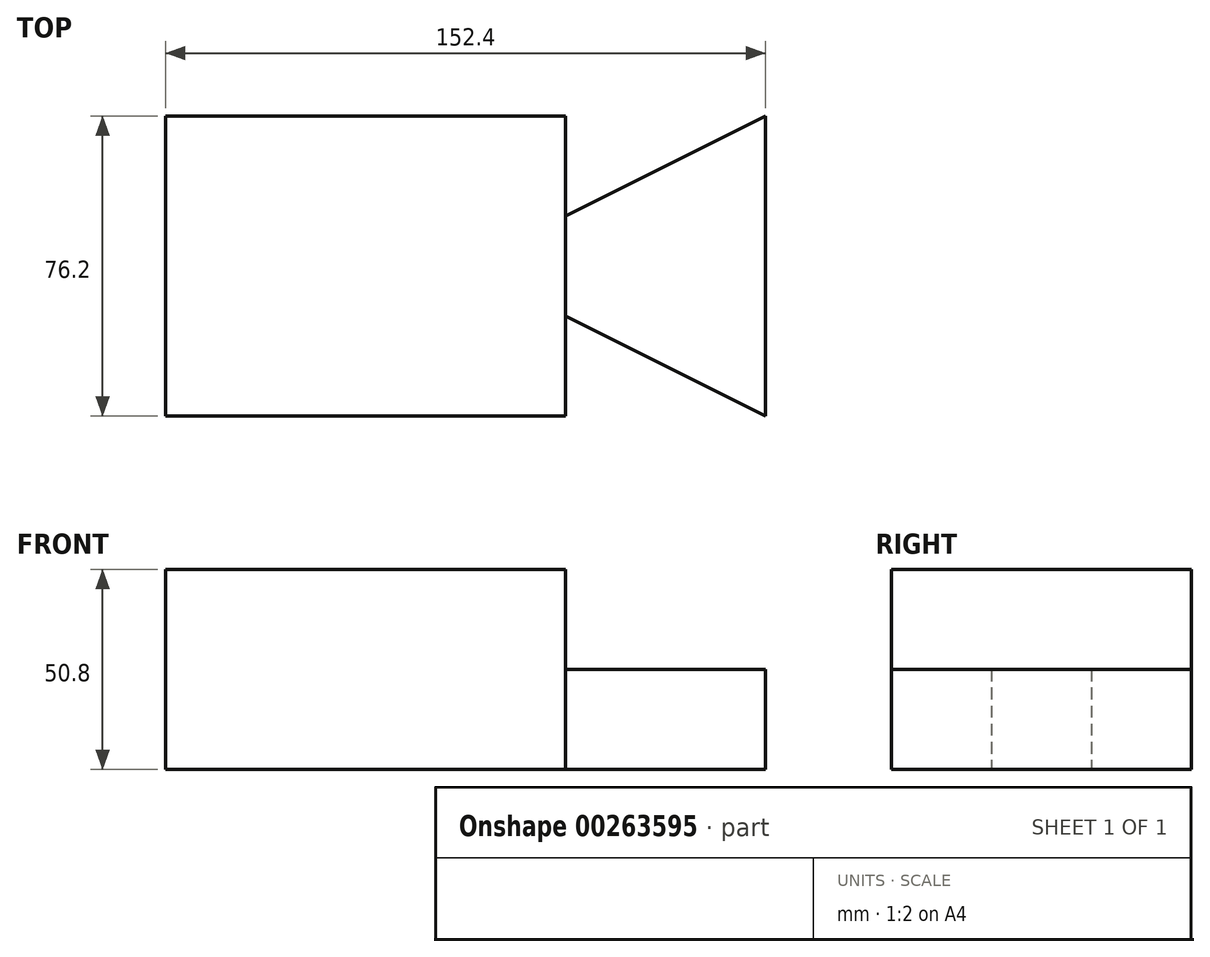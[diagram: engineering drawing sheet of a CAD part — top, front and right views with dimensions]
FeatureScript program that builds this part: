
annotation { "Feature Type Name" : "Feature", "Feature Type Description" : "" }
export const myFeature = defineFeature(function(context is Context, id is Id, definition is map)
    precondition{}
    {
        {
            var Q0;
            Q0=qCreatedBy(makeId("Front.planeOp"),FACE);
            var sketch = newSketch(context, id + "F0", { "sketchPlane" : qUnion([Q0])});
            skLineSegment(sketch, "E0", {"start": v(-72.92, 0) * mm, "end": v(-72.92, 50.8) * mm});
            skLineSegment(sketch, "E1", {"start": v(-72.92, 50.8) * mm, "end": v(28.68, 50.8) * mm});
            skLineSegment(sketch, "E2", {"start": v(-72.92, 0) * mm, "end": v(28.68, 0) * mm});
            skLineSegment(sketch, "E3", {"start": v(28.68, 0) * mm, "end": v(28.68, 25.4) * mm});
            skLineSegment(sketch, "E4", {"start": v(28.68, 50.8) * mm, "end": v(28.68, 25.4) * mm});
            skLineSegment(sketch, "E5", {"start": v(28.68, 25.4) * mm, "end": v(28.68, 50.8) * mm});
            skSolve(sketch);
        }
        {
            var Q0;
            Q0 = qSketchRegion(id + "F0", true);
            extrude(context, id + "F1", {"entities" : qUnion([Q0]), "depth" : 76.2 * mm});
        }
        {
            var Q0;
            Q0=makeQuery(id+"F1.opExtrude","SWEPT_FACE",FACE,{"disambiguationData":[OSD([sQuery(id+"F0.wireOp",EDGE,"E2")])]});
            var sketch = newSketch(context, id + "F2", { "sketchPlane" : qUnion([Q0])});
            skLineSegment(sketch, "E6", {"start": v(28.68, 0) * mm, "end": v(28.68, 25.4) * mm, "construction": true});
            skLineSegment(sketch, "E7", {"start": v(28.68, 76.2) * mm, "end": v(28.68, 50.8) * mm, "construction": true});
            skLineSegment(sketch, "E8", {"start": v(28.68, 76.2) * mm, "end": v(79.48, 76.2) * mm, "construction": true});
            skLineSegment(sketch, "E9", {"start": v(79.48, 76.2) * mm, "end": v(79.48, 0) * mm});
            skLineSegment(sketch, "E10", {"start": v(28.68, 50.8) * mm, "end": v(79.48, 76.2) * mm});
            skLineSegment(sketch, "E11", {"start": v(28.68, 25.4) * mm, "end": v(79.48, 0) * mm});
            skLineSegment(sketch, "E12", {"start": v(28.68, 50.8) * mm, "end": v(28.68, 25.4) * mm});
            skSolve(sketch);
        }
        {
            var Q0;
            Q0=makeQuery(id+"F2.imprint","IMPRINT",FACE,{"disambiguationData":[TD([[makeQuery(id+"F2.imprint","IMPRINT",EDGE,{"derivedFrom":sQuery(id+"F2.wireOp",EDGE,"E9")}),-1.0]])]});
            extrude(context, id + "F3", {"entities" : qUnion([Q0]), "oppositeDirection" : true, "depth" : 25.4 * mm});
        }
    });
